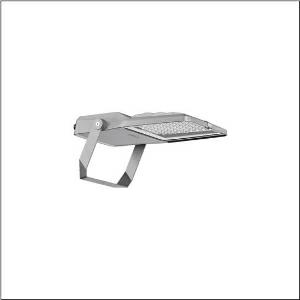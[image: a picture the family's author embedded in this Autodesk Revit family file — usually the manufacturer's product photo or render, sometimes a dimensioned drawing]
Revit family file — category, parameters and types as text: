
# Revit family: floodlight_fl_21_iq_mini___rs12_5xa7772d3b1a_ff90
name_source: partatom
category: Lighting Fixtures
units: mm (PartAtom-declared; Revit-internal decimal feet)

## family parameters
Cut with Voids When Loaded = No
Host = Face
Light Source = No
Part Type = Normal
Room Calculation Point = No
Round Connector Dimension = Use Diameter
Shared = No

## types (1)
- --- (1 x LED, 15500 lm, 143 W, 3000K)
    Apparent Load = 143 VA
    CIE Flux Codes = 79 92 99 100 100
    Color Rendering = 80
    Color Temperature = 3000K
    Default Elevation = 1800 mm
    Description = Floodlight FL 21 iQ mini, floodlight, primary light control with lens, of PMMA, primary optical cover: protective disc, of toughened safety glass, transparent, light distribution: RS12, light emission: direct distribution, installation type: surface-mounted, LED, High Power LED, rated luminous flux: 15.500lm, luminous efficacy: 108lm/W, light colour: 830, colour temperature: 3000K, control gear: iQ Street-Remote/DALI, control: Street-Remote, Auto-Match, Temp-Guard, Night-Set, Smart-Wire, Desk-Remote (wireless, voltage-free reading and setting of iQ features in the workshop via application-optimized NFC function/RFID function), optimised constant luminous flux control (CLO 2.0), with terminal, 6-pole, mains connection: 220..240V, AC, 50/60Hz, start of lifetime: 143W, end of service life: 152W, reduction: 61W, luminaire housing, of diecast aluminium, powder-coated, Siteco® metallic grey (DB 702S), corrosivity category C5 mid according to DIN EN ISO 12944, suitable for swimming pools, chlorine-resistant, sealing non-destructively replaceable, mounting bracket, of steel, galvanised, powder-coated, Siteco® metallic grey (DB 702S), protection rating (complete): IP66, insulation class (complete): insulation class II (safety insulation), certification: CE, ENEC, VDE, protection symbol: D, impact resistance: IK08, permissible operating ambient temperature: -40..+40°C, permissible operating ambient temperature for outdoor applications: -40..+50°C, standard: DIN EN 12944, LABS conformity tested according to VDMA 24364:2018-05, packaging unit: 1 piece

Light Distribution: RS12
    Height = 70 mm
    Lamp = 1 x LED
    Lamp Light Flux = 15500 lm
    Lamp Power = 143 W
    Lamp count = 1
    Length = 485 mm
    Luminous efficacy = 108 lm/W
    Manufacturer = Siteco
    ModVariant = No
    Model = 5XA7772D3B1A
    Number of Poles = 1
    OnlyDefault = Yes
    Power Factor = 1
    Product Name = Floodlight FL 21 iQ mini | RS12
    Product group = floodlight | pylon annexe
    ProductGroupID = 6201
    Protection Class = Protection class II
    Protection Degree = IP 66
    RLX_Detail_Level = 1
    RLX_Emergency_Light_Flux = 0 lm
    RLX_Emergency_Type = 0
    RLX_Emergency_Type_DB = No
    RlxData = <blob elided: 91429 chars, md5=939f2d8c>
    Socket = socket
    Standby Power = 0 W
    System Light Flux = 15500 lm
    System Power = 143 W
    Type Comments = factory setting: luminous flux: 100 % | dim-lin: 254 | 730 mA
    Type Image = l_1006845.jpg
    URL = http://relux.com
    VarID = @adj_188803
    Voltage = 0 V
    Weight = 0.00 kg
    Width = 337 mm

## geometry (parser evidence)
native form markers: Blend x4, Sweep x12
no freeform markers — native parametric forms only
